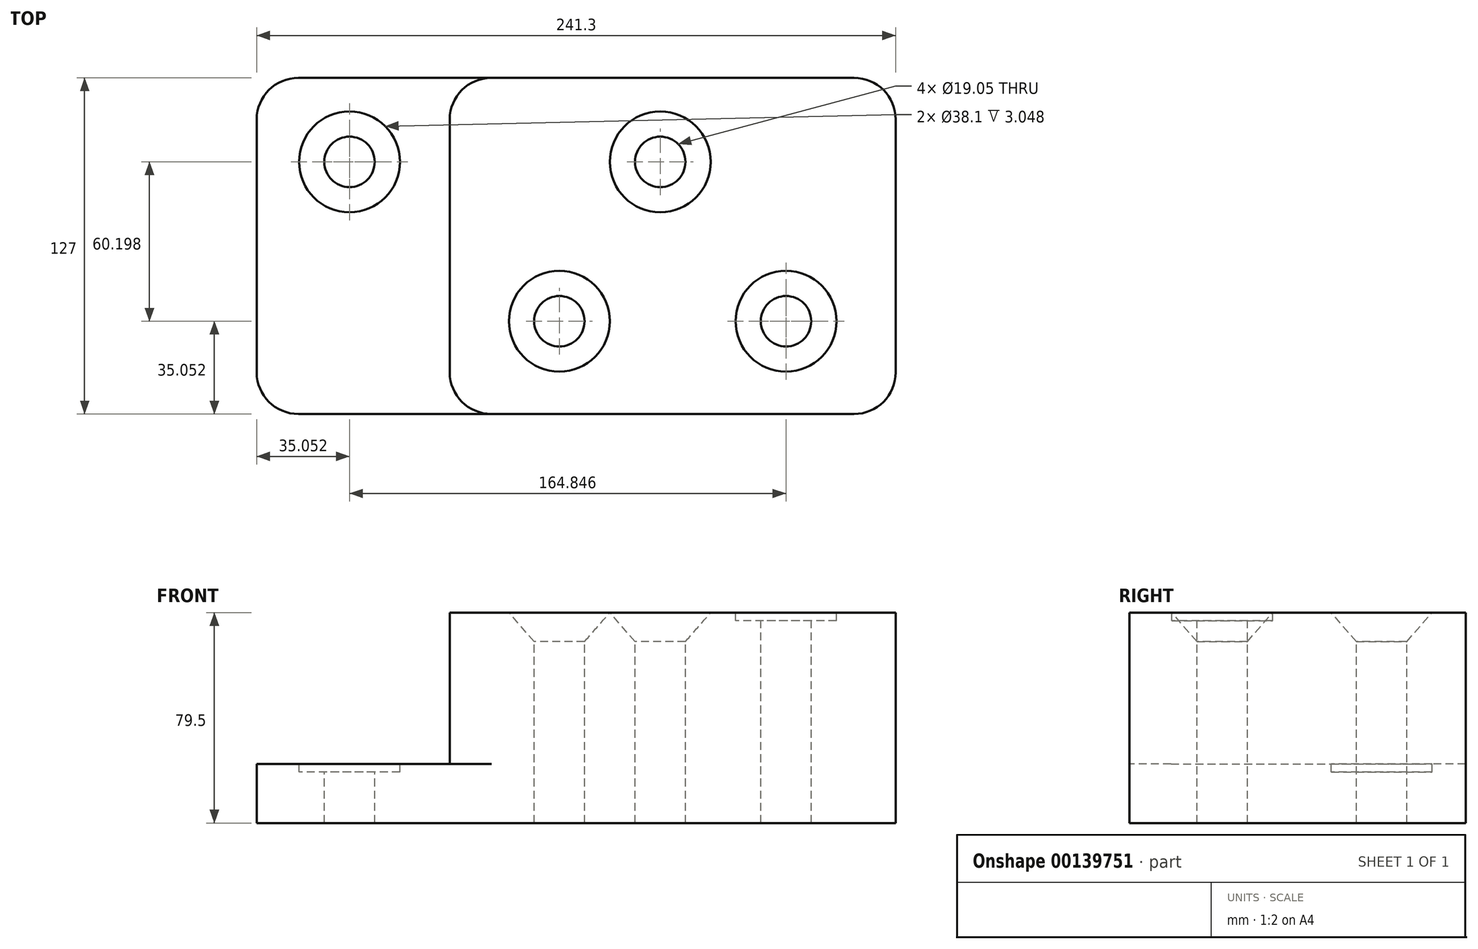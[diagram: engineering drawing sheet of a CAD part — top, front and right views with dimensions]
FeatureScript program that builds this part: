
annotation { "Feature Type Name" : "Feature", "Feature Type Description" : "" }
export const myFeature = defineFeature(function(context is Context, id is Id, definition is map)
    precondition{}
    {
        {
            var Q0;
            Q0=qCreatedBy(makeId("Top.planeOp"),FACE);
            var sketch = newSketch(context, id + "F0", { "sketchPlane" : qUnion([Q0])});
            skLineSegment(sketch, "E0.bottom", {"start": v(-15.75, -63.5) * mm, "end": v(-152.65, -63.5) * mm});
            skLineSegment(sketch, "E0.top", {"start": v(-15.75, 63.5) * mm, "end": v(-152.65, 63.5) * mm});
            skLineSegment(sketch, "E0.left", {"start": v(0, -47.75) * mm, "end": v(0, 47.75) * mm});
            skLineSegment(sketch, "E0.right", {"start": v(-241.3, -47.75) * mm, "end": v(-241.3, 47.75) * mm});
            skLineSegment(sketch, "E1", {"start": v(-168.4, 47.75) * mm, "end": v(-168.4, -47.75) * mm});
            skPoint(sketch, "E2.newPointB", {"position": v(-241.3, 63.5) * mm});
            skArc(sketch, "E2.filletArc", {"start": v(-152.65, 63.5) * mm, "mid": v(-163.79, 58.89) * mm, "end": v(-168.4, 47.75) * mm});
            skLineSegment(sketch, "E3", {"start": v(-225.55, 63.5) * mm, "end": v(-152.65, 63.5) * mm});
            skPoint(sketch, "E4.visualSharp", {"position": v(0, 63.5) * mm});
            skArc(sketch, "E4.filletArc", {"start": v(0, 47.75) * mm, "mid": v(-4.61, 58.89) * mm, "end": v(-15.75, 63.5) * mm});
            skPoint(sketch, "E5.visualSharp", {"position": v(0, -63.5) * mm});
            skArc(sketch, "E5.filletArc", {"start": v(-15.75, -63.5) * mm, "mid": v(-4.61, -58.89) * mm, "end": v(0, -47.75) * mm});
            skArc(sketch, "E6.filletArc", {"start": v(-168.4, -47.75) * mm, "mid": v(-163.79, -58.89) * mm, "end": v(-152.65, -63.5) * mm});
            skLineSegment(sketch, "E7", {"start": v(-225.55, -63.5) * mm, "end": v(-152.65, -63.5) * mm});
            skArc(sketch, "E8.filletArc", {"start": v(-225.55, 63.5) * mm, "mid": v(-236.69, 58.89) * mm, "end": v(-241.3, 47.75) * mm});
            skPoint(sketch, "E9.visualSharp", {"position": v(-241.3, -63.5) * mm});
            skArc(sketch, "E9.filletArc", {"start": v(-241.3, -47.75) * mm, "mid": v(-236.69, -58.89) * mm, "end": v(-225.55, -63.5) * mm});
            skSolve(sketch);
        }
        {
            var Q0;
            Q0 = qSketchRegion(id + "F0", true);
            extrude(context, id + "F1", {"entities" : qUnion([Q0]), "depth" : 22.35 * mm});
        }
        {
            var Q0;
            {var subQ0=sQuery(id+"F0.wireOp",EDGE,"E0.left");Q0=makeQuery(id+"F0.imprint","IMPRINT",FACE,{"disambiguationData":[TD([[makeQuery(id+"F0.imprint","IMPRINT",EDGE,{"derivedFrom":subQ0}),1.0]])]});}
            extrude(context, id + "F2", {"entities" : qUnion([Q0]), "operationType" : NewBodyOperationType.ADD, "depth" : 79.5 * mm});
        }
        {
            var Q0;
            Q0=makeQuery(id+"F2.opExtrude","CAP_FACE",FACE,{"disambiguationData":[OSD([sQuery(id+"F0.wireOp",EDGE,"E0.bottom"),sQuery(id+"F0.wireOp",EDGE,"E0.top"),sQuery(id+"F0.wireOp",EDGE,"E0.left"),sQuery(id+"F0.wireOp",EDGE,"E1"),sQuery(id+"F0.wireOp",EDGE,"E2.filletArc"),sQuery(id+"F0.wireOp",EDGE,"E4.filletArc"),sQuery(id+"F0.wireOp",EDGE,"E5.filletArc"),sQuery(id+"F0.wireOp",EDGE,"E6.filletArc")])],"isStart":false});
            var sketch = newSketch(context, id + "F3", { "sketchPlane" : qUnion([Q0])});
            skPoint(sketch, "E10", {"position": v(-41.4, -28.45) * mm});
            skPoint(sketch, "E11", {"position": v(-127, -28.45) * mm});
            skPoint(sketch, "E12", {"position": v(-88.9, 31.75) * mm});
            skPoint(sketch, "E13", {"position": v(-206.25, 31.75) * mm});
            skSolve(sketch);
        }
        {
            var Q0;
            Q0=sQuery(id+"F3.wireOp",VERTEX,"E12");
            var Q1;
            Q1=sQuery(id+"F3.wireOp",VERTEX,"E11");
            var Q2;
            Q2=makeQuery(id+"F1.opExtrude","SWEPT_BODY",BODY,{"disambiguationData":[OSD([sQuery(id+"F0.wireOp",EDGE,"E0.bottom"),sQuery(id+"F0.wireOp",EDGE,"E0.top"),sQuery(id+"F0.wireOp",EDGE,"E0.left"),sQuery(id+"F0.wireOp",EDGE,"E0.right"),sQuery(id+"F0.wireOp",EDGE,"E3"),sQuery(id+"F0.wireOp",EDGE,"E4.filletArc"),sQuery(id+"F0.wireOp",EDGE,"E5.filletArc"),sQuery(id+"F0.wireOp",EDGE,"E7"),sQuery(id+"F0.wireOp",EDGE,"E8.filletArc"),sQuery(id+"F0.wireOp",EDGE,"E9.filletArc")])]});
            hole(context, id + "F4", {"style" : HoleStyle.C_SINK, "endStyle" : HoleEndStyle.THROUGH, "holeDiameter" : 19.05 * mm, "cSinkDiameter" : 38.1 * mm, "cSinkAngle" : 82 * degree, "locations" : qUnion([Q0, Q1]), "scope" : qUnion([Q2]), "isTappedThrough" : true});
        }
        {
            var Q0;
            Q0=makeQuery(id+"F2.opExtrude","CAP_FACE",FACE,{"disambiguationData":[OSD([sQuery(id+"F0.wireOp",EDGE,"E0.bottom"),sQuery(id+"F0.wireOp",EDGE,"E0.top"),sQuery(id+"F0.wireOp",EDGE,"E0.left"),sQuery(id+"F0.wireOp",EDGE,"E1"),sQuery(id+"F0.wireOp",EDGE,"E2.filletArc"),sQuery(id+"F0.wireOp",EDGE,"E4.filletArc"),sQuery(id+"F0.wireOp",EDGE,"E5.filletArc"),sQuery(id+"F0.wireOp",EDGE,"E6.filletArc")])],"isStart":false});
            var sketch = newSketch(context, id + "F5", { "sketchPlane" : qUnion([Q0])});
            skPoint(sketch, "E14", {"position": v(-206.25, 31.75) * mm});
            skPoint(sketch, "E15", {"position": v(-41.4, -28.45) * mm});
            skSolve(sketch);
        }
        {
            var Q0;
            Q0=sQuery(id+"F5.wireOp",VERTEX,"E14");
            var Q1;
            Q1=sQuery(id+"F5.wireOp",VERTEX,"E15");
            var Q2;
            Q2=makeQuery(id+"F1.opExtrude","SWEPT_BODY",BODY,{"disambiguationData":[OSD([sQuery(id+"F0.wireOp",EDGE,"E0.bottom"),sQuery(id+"F0.wireOp",EDGE,"E0.top"),sQuery(id+"F0.wireOp",EDGE,"E0.left"),sQuery(id+"F0.wireOp",EDGE,"E0.right"),sQuery(id+"F0.wireOp",EDGE,"E3"),sQuery(id+"F0.wireOp",EDGE,"E4.filletArc"),sQuery(id+"F0.wireOp",EDGE,"E5.filletArc"),sQuery(id+"F0.wireOp",EDGE,"E7"),sQuery(id+"F0.wireOp",EDGE,"E8.filletArc"),sQuery(id+"F0.wireOp",EDGE,"E9.filletArc")])]});
            hole(context, id + "F6", {"style" : HoleStyle.C_BORE, "endStyle" : HoleEndStyle.THROUGH, "holeDiameter" : 19.05 * mm, "cBoreDiameter" : 38.1 * mm, "cBoreDepth" : 3.05 * mm, "locations" : qUnion([Q0, Q1]), "scope" : qUnion([Q2]), "isTappedThrough" : true});
        }
    });
